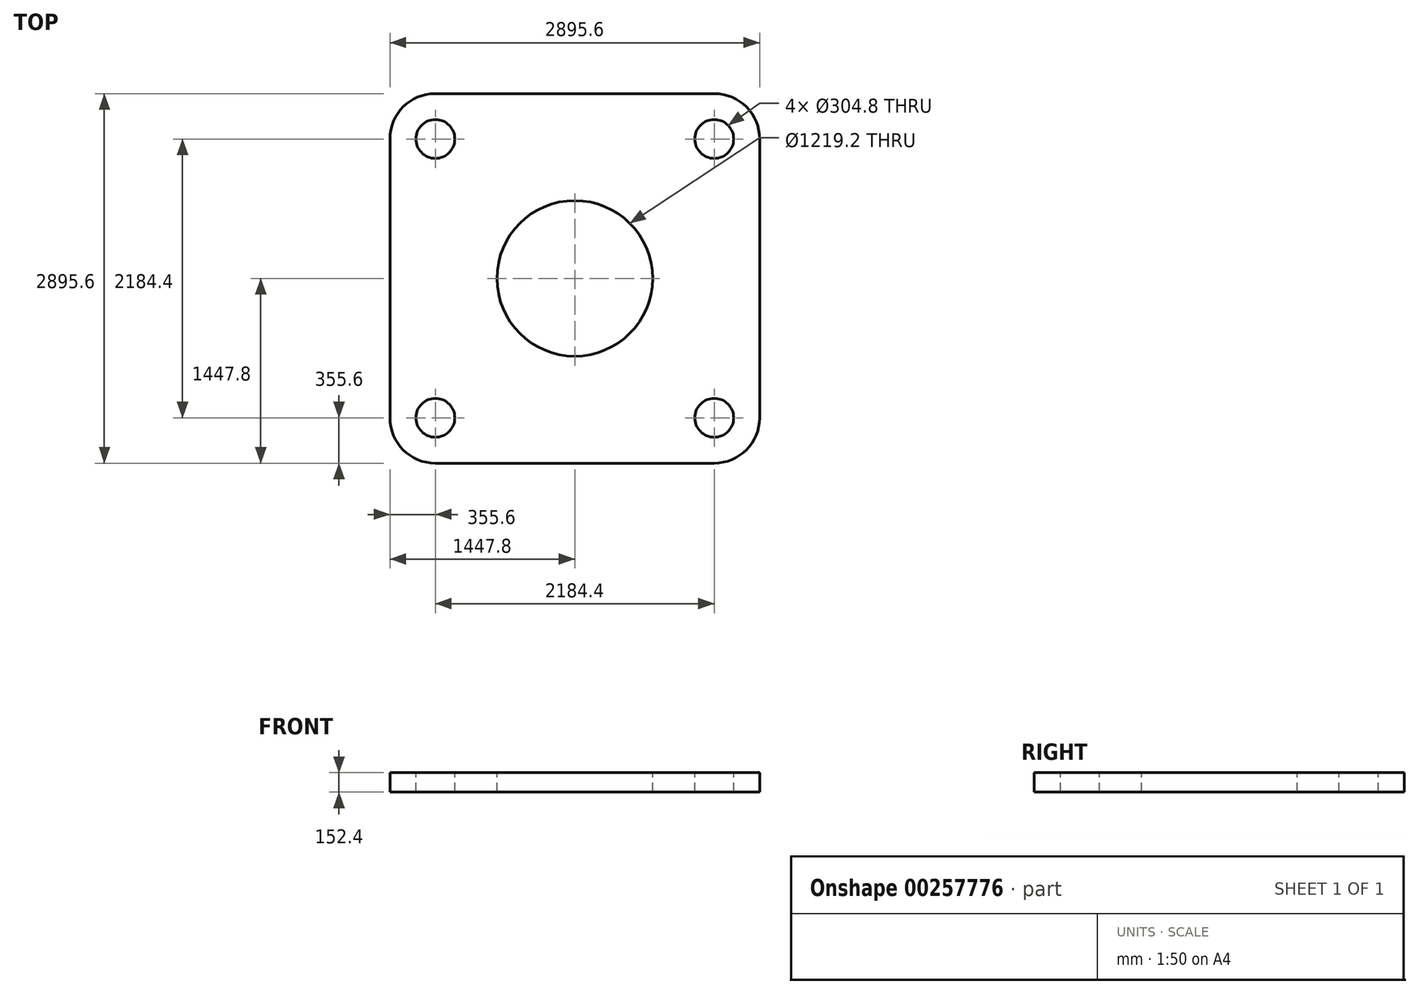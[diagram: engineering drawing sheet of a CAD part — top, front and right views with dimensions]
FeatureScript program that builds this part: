
annotation { "Feature Type Name" : "Feature", "Feature Type Description" : "" }
export const myFeature = defineFeature(function(context is Context, id is Id, definition is map)
    precondition{}
    {
        {
            var Q0;
            Q0=qCreatedBy(makeId("Top.planeOp"),FACE);
            var sketch = newSketch(context, id + "F0", { "sketchPlane" : qUnion([Q0])});
            skLineSegment(sketch, "E0.bottom", {"start": v(1092.2, -1447.8) * mm, "end": v(-1092.2, -1447.8) * mm});
            skLineSegment(sketch, "E0.top", {"start": v(1092.2, 1447.8) * mm, "end": v(-1092.2, 1447.8) * mm});
            skLineSegment(sketch, "E0.left", {"start": v(1447.8, -1092.2) * mm, "end": v(1447.8, 1092.2) * mm});
            skLineSegment(sketch, "E0.right", {"start": v(-1447.8, -1092.2) * mm, "end": v(-1447.8, 1092.2) * mm});
            skPoint(sketch, "E0.middle", {"position": v(0, 0) * mm});
            skPoint(sketch, "E1.visualSharp", {"position": v(-1447.8, 1447.8) * mm});
            skArc(sketch, "E1.filletArc", {"start": v(-1441.45, 1447.8) * mm, "mid": v(-1445.94, 1445.94) * mm, "end": v(-1447.8, 1441.45) * mm});
            skPoint(sketch, "E2.visualSharp", {"position": v(1447.8, 1447.8) * mm});
            skArc(sketch, "E2.filletArc", {"start": v(1447.8, 1441.45) * mm, "mid": v(1445.94, 1445.94) * mm, "end": v(1441.45, 1447.8) * mm});
            skArc(sketch, "E3.filletArc", {"start": v(-1092.2, 1447.8) * mm, "mid": v(-1343.65, 1343.65) * mm, "end": v(-1447.8, 1092.2) * mm});
            skArc(sketch, "E4.filletArc", {"start": v(1447.8, 1092.2) * mm, "mid": v(1343.65, 1343.65) * mm, "end": v(1092.2, 1447.8) * mm});
            skPoint(sketch, "E5.visualSharp", {"position": v(1447.8, -1447.8) * mm});
            skArc(sketch, "E5.filletArc", {"start": v(1092.2, -1447.8) * mm, "mid": v(1343.65, -1343.65) * mm, "end": v(1447.8, -1092.2) * mm});
            skPoint(sketch, "E6.visualSharp", {"position": v(-1447.8, -1447.8) * mm});
            skArc(sketch, "E6.filletArc", {"start": v(-1447.8, -1092.2) * mm, "mid": v(-1343.65, -1343.65) * mm, "end": v(-1092.2, -1447.8) * mm});
            skCircle(sketch, "E7", {"center": v(0, 0) * mm, "radius": 609.6 * mm});
            skCircle(sketch, "E8", {"center": v(-1092.2, 1092.2) * mm, "radius": 152.4 * mm});
            skCircle(sketch, "E9", {"center": v(1092.2, 1092.2) * mm, "radius": 152.4 * mm});
            skCircle(sketch, "E10", {"center": v(1092.2, -1092.2) * mm, "radius": 152.4 * mm});
            skCircle(sketch, "E11", {"center": v(-1092.2, -1092.2) * mm, "radius": 152.4 * mm});
            skSolve(sketch);
        }
        {
            var Q0;
            Q0 = qSketchRegion(id + "F0", true);
            extrude(context, id + "F1", {"entities" : qUnion([Q0]), "oppositeDirection" : true, "depth" : 152.4 * mm});
        }
    });
